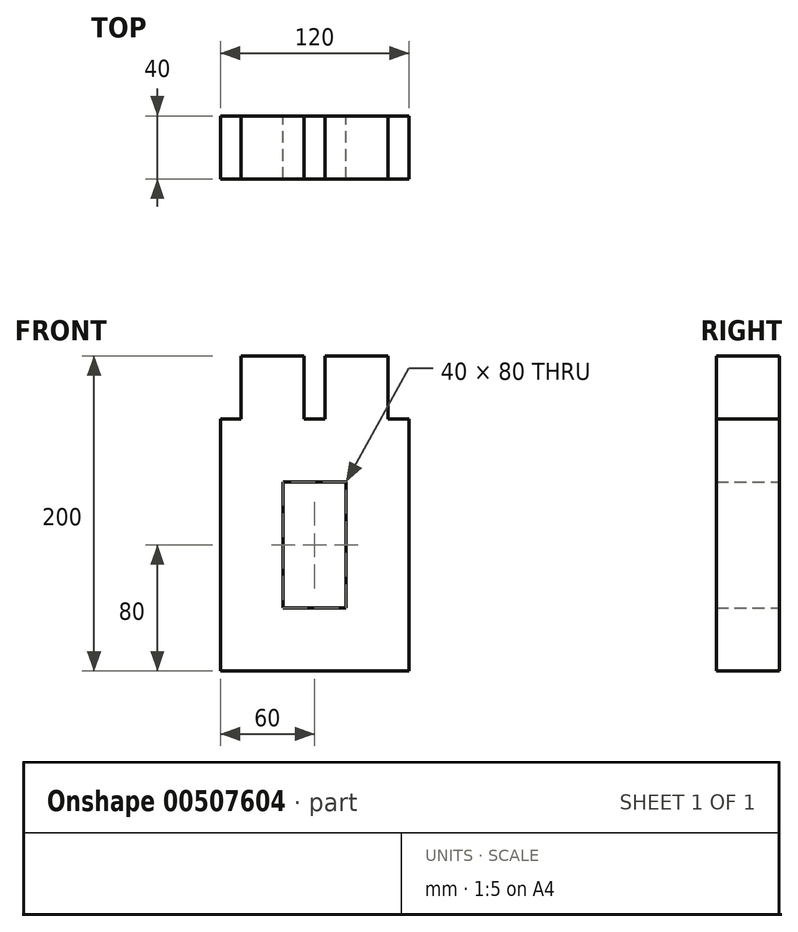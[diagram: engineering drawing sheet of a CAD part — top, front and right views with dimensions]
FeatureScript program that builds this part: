
annotation { "Feature Type Name" : "Feature", "Feature Type Description" : "" }
export const myFeature = defineFeature(function(context is Context, id is Id, definition is map)
    precondition{}
    {
        {
            var Q0;
            Q0=qCreatedBy(makeId("Front.planeOp"),FACE);
            var sketch = newSketch(context, id + "F0", { "sketchPlane" : qUnion([Q0])});
            skLineSegment(sketch, "E0.bottom", {"start": v(60, 100) * mm, "end": v(-60, 100) * mm});
            skLineSegment(sketch, "E0.top", {"start": v(60, -100) * mm, "end": v(-60, -100) * mm});
            skLineSegment(sketch, "E0.left", {"start": v(60, 100) * mm, "end": v(60, -100) * mm});
            skLineSegment(sketch, "E0.right", {"start": v(-60, 100) * mm, "end": v(-60, -100) * mm});
            skPoint(sketch, "E0.middle", {"position": v(0, 0) * mm});
            skLineSegment(sketch, "E1", {"start": v(-20, 100) * mm, "end": v(-20, -100) * mm});
            skLineSegment(sketch, "E2", {"start": v(20, 100) * mm, "end": v(20, -100) * mm});
            skLineSegment(sketch, "E3", {"start": v(60, 60) * mm, "end": v(-60, 60) * mm});
            skLineSegment(sketch, "E4", {"start": v(60, 20) * mm, "end": v(-60, 20) * mm});
            skLineSegment(sketch, "E5", {"start": v(60, -20) * mm, "end": v(-60, -20) * mm});
            skLineSegment(sketch, "E6", {"start": v(60, -60) * mm, "end": v(-60, -60) * mm});
            skLineSegment(sketch, "E7", {"start": v(-6.67, 100) * mm, "end": v(-6.67, 60) * mm});
            skLineSegment(sketch, "E8", {"start": v(-46.67, 100) * mm, "end": v(-46.67, 60) * mm});
            skLineSegment(sketch, "E9.MirrorCS", {"start": v(6.67, 100) * mm, "end": v(6.67, 60) * mm});
            skLineSegment(sketch, "E10.MirrorCS", {"start": v(46.67, 100) * mm, "end": v(46.67, 60) * mm});
            skSolve(sketch);
        }
        {
            var Q0;
            {var subQ3=sQuery(id+"F0.wireOp",EDGE,"E8");Q0=makeQuery(id+"F0.imprint","IMPRINT",FACE,{"disambiguationData":[TD([[makeQuery(id+"F0.imprint","IMPRINT",EDGE,{"derivedFrom":subQ3}),1.0]])]});}
            var Q1;
            {var subQ3=sQuery(id+"F0.wireOp",EDGE,"E7");Q1=makeQuery(id+"F0.imprint","IMPRINT",FACE,{"disambiguationData":[TD([[makeQuery(id+"F0.imprint","IMPRINT",EDGE,{"derivedFrom":subQ3}),-1.0]])]});}
            var Q2;
            {var subQ3=sQuery(id+"F0.wireOp",EDGE,"E9.MirrorCS");Q2=makeQuery(id+"F0.imprint","IMPRINT",FACE,{"disambiguationData":[TD([[makeQuery(id+"F0.imprint","IMPRINT",EDGE,{"derivedFrom":subQ3}),1.0]])]});}
            var Q3;
            {var subQ3=sQuery(id+"F0.wireOp",EDGE,"E10.MirrorCS");Q3=makeQuery(id+"F0.imprint","IMPRINT",FACE,{"disambiguationData":[TD([[makeQuery(id+"F0.imprint","IMPRINT",EDGE,{"derivedFrom":subQ3}),-1.0]])]});}
            var Q4;
            {var subQ0=sQuery(id+"F0.wireOp",EDGE,"E3");var subQ4=sQuery(id+"F0.wireOp",EDGE,"E0.right");var subQ5=makeQuery(id+"F0.imprint","INTERSECT",VERTEX,{"derivedFrom":[subQ4,subQ0]});Q4=makeQuery(id+"F0.imprint","IMPRINT",FACE,{"disambiguationData":[TD([[makeQuery(id+"F0.imprint","IMPRINT",EDGE,{"disambiguationData":[TD([[subQ5,-1.0]])],"derivedFrom":subQ4}),1.0]])]});}
            var Q5;
            {var subQ0=sQuery(id+"F0.wireOp",EDGE,"E3");var subQ5=sQuery(id+"F0.wireOp",EDGE,"E1");var subQ6=makeQuery(id+"F0.imprint","INTERSECT",VERTEX,{"derivedFrom":[subQ5,subQ0]});Q5=makeQuery(id+"F0.imprint","IMPRINT",FACE,{"disambiguationData":[TD([[makeQuery(id+"F0.imprint","IMPRINT",EDGE,{"disambiguationData":[TD([[subQ6,-1.0]])],"derivedFrom":subQ5}),1.0]])]});}
            var Q6;
            {var subQ0=sQuery(id+"F0.wireOp",EDGE,"E3");var subQ1=sQuery(id+"F0.wireOp",EDGE,"E0.left");var subQ2=makeQuery(id+"F0.imprint","INTERSECT",VERTEX,{"derivedFrom":[subQ1,subQ0]});Q6=makeQuery(id+"F0.imprint","IMPRINT",FACE,{"disambiguationData":[TD([[makeQuery(id+"F0.imprint","IMPRINT",EDGE,{"disambiguationData":[TD([[subQ2,-1.0]])],"derivedFrom":subQ1}),-1.0]])]});}
            var Q7;
            {var subQ0=sQuery(id+"F0.wireOp",EDGE,"E4");var subQ1=sQuery(id+"F0.wireOp",EDGE,"E0.left");var subQ2=makeQuery(id+"F0.imprint","INTERSECT",VERTEX,{"derivedFrom":[subQ1,subQ0]});Q7=makeQuery(id+"F0.imprint","IMPRINT",FACE,{"disambiguationData":[TD([[makeQuery(id+"F0.imprint","IMPRINT",EDGE,{"disambiguationData":[TD([[subQ2,-1.0]])],"derivedFrom":subQ1}),-1.0]])]});}
            var Q8;
            {var subQ0=sQuery(id+"F0.wireOp",EDGE,"E5");var subQ1=sQuery(id+"F0.wireOp",EDGE,"E0.left");var subQ2=makeQuery(id+"F0.imprint","INTERSECT",VERTEX,{"derivedFrom":[subQ1,subQ0]});Q8=makeQuery(id+"F0.imprint","IMPRINT",FACE,{"disambiguationData":[TD([[makeQuery(id+"F0.imprint","IMPRINT",EDGE,{"disambiguationData":[TD([[subQ2,-1.0]])],"derivedFrom":subQ1}),-1.0]])]});}
            var Q9;
            {var subQ0=sQuery(id+"F0.wireOp",EDGE,"E0.left");var subQ1=sQuery(id+"F0.wireOp",EDGE,"E0.top");var subQ2=makeQuery(id+"F0.imprint","INTERSECT",VERTEX,{"derivedFrom":[subQ1,subQ0]});Q9=makeQuery(id+"F0.imprint","IMPRINT",FACE,{"disambiguationData":[TD([[makeQuery(id+"F0.imprint","IMPRINT",EDGE,{"disambiguationData":[TD([[subQ2,-1.0]])],"derivedFrom":subQ1}),-1.0]])]});}
            var Q10;
            {var subQ0=sQuery(id+"F0.wireOp",EDGE,"E1");var subQ1=sQuery(id+"F0.wireOp",EDGE,"E0.top");var subQ2=makeQuery(id+"F0.imprint","INTERSECT",VERTEX,{"derivedFrom":[subQ1,subQ0]});Q10=makeQuery(id+"F0.imprint","IMPRINT",FACE,{"disambiguationData":[TD([[makeQuery(id+"F0.imprint","IMPRINT",EDGE,{"disambiguationData":[TD([[subQ2,1.0]])],"derivedFrom":subQ1}),-1.0]])]});}
            var Q11;
            {var subQ0=sQuery(id+"F0.wireOp",EDGE,"E0.right");var subQ1=sQuery(id+"F0.wireOp",EDGE,"E0.top");var subQ2=makeQuery(id+"F0.imprint","INTERSECT",VERTEX,{"derivedFrom":[subQ1,subQ0]});Q11=makeQuery(id+"F0.imprint","IMPRINT",FACE,{"disambiguationData":[TD([[makeQuery(id+"F0.imprint","IMPRINT",EDGE,{"disambiguationData":[TD([[subQ2,1.0]])],"derivedFrom":subQ1}),-1.0]])]});}
            var Q12;
            {var subQ0=sQuery(id+"F0.wireOp",EDGE,"E5");var subQ1=sQuery(id+"F0.wireOp",EDGE,"E0.right");var subQ2=makeQuery(id+"F0.imprint","INTERSECT",VERTEX,{"derivedFrom":[subQ1,subQ0]});Q12=makeQuery(id+"F0.imprint","IMPRINT",FACE,{"disambiguationData":[TD([[makeQuery(id+"F0.imprint","IMPRINT",EDGE,{"disambiguationData":[TD([[subQ2,-1.0]])],"derivedFrom":subQ1}),1.0]])]});}
            var Q13;
            {var subQ0=sQuery(id+"F0.wireOp",EDGE,"E4");var subQ1=sQuery(id+"F0.wireOp",EDGE,"E0.right");var subQ2=makeQuery(id+"F0.imprint","INTERSECT",VERTEX,{"derivedFrom":[subQ1,subQ0]});Q13=makeQuery(id+"F0.imprint","IMPRINT",FACE,{"disambiguationData":[TD([[makeQuery(id+"F0.imprint","IMPRINT",EDGE,{"disambiguationData":[TD([[subQ2,-1.0]])],"derivedFrom":subQ1}),1.0]])]});}
            extrude(context, id + "F1", {"entities" : qUnion([Q0, Q1, Q2, Q3, Q4, Q5, Q6, Q7, Q8, Q9, Q10, Q11, Q12, Q13]), "depth" : 40 * mm, "offsetDistance" : 25 * mm});
        }
    });
